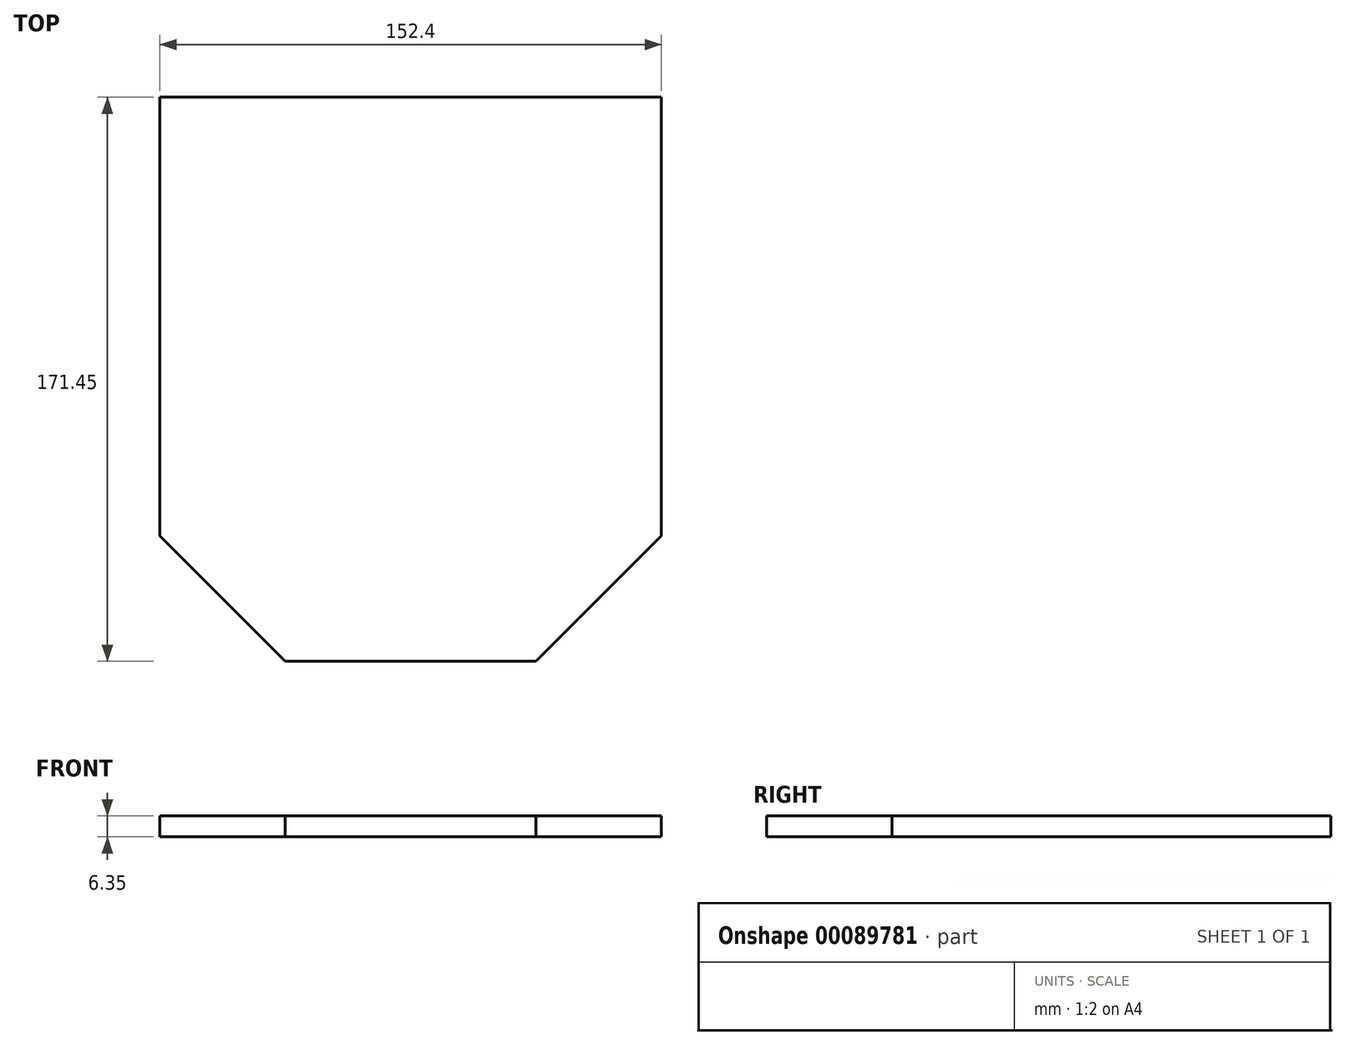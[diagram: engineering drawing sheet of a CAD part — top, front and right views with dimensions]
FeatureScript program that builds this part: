
annotation { "Feature Type Name" : "Feature", "Feature Type Description" : "" }
export const myFeature = defineFeature(function(context is Context, id is Id, definition is map)
    precondition{}
    {
        {
            var Q0;
            Q0=qCreatedBy(makeId("Top.planeOp"),FACE);
            var sketch = newSketch(context, id + "F0", { "sketchPlane" : qUnion([Q0])});
            skLineSegment(sketch, "E0.bottom", {"start": v(38.1, 0) * mm, "end": v(114.3, 0) * mm});
            skLineSegment(sketch, "E0.top", {"start": v(0, 171.45) * mm, "end": v(152.4, 171.45) * mm});
            skLineSegment(sketch, "E0.left", {"start": v(0, 38.1) * mm, "end": v(0, 171.45) * mm});
            skLineSegment(sketch, "E0.right", {"start": v(152.4, 38.1) * mm, "end": v(152.4, 171.45) * mm});
            skLineSegment(sketch, "E1", {"start": v(114.3, 0) * mm, "end": v(152.4, 38.1) * mm});
            skLineSegment(sketch, "E2", {"start": v(0, 38.1) * mm, "end": v(38.1, 0) * mm});
            skPoint(sketch, "E3.orphan", {"position": v(0, 0) * mm});
            skPoint(sketch, "E4.orphan", {"position": v(152.4, 0) * mm});
            skSolve(sketch);
        }
        {
            var Q0;
            Q0=makeQuery(id+"F0.imprint","IMPRINT",FACE,{"disambiguationData":[TD([[makeQuery(id+"F0.imprint","IMPRINT",EDGE,{"derivedFrom":sQuery(id+"F0.wireOp",EDGE,"E0.bottom")}),1.0]])]});
            extrude(context, id + "F1", {"entities" : qUnion([Q0]), "depth" : 6.35 * mm});
        }
    });
